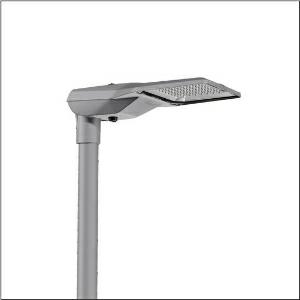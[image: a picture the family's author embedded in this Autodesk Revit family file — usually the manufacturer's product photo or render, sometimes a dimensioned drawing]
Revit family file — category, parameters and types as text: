
# Revit family: streetlight_sl_21_iq_midi___pl52_5xe3h31y08mb_cc6d
name_source: partatom
category: Lighting Fixtures
units: mm (PartAtom-declared; Revit-internal decimal feet)

## family parameters
Cut with Voids When Loaded = No
Host = Face
Light Source = No
Part Type = Normal
Room Calculation Point = No
Round Connector Dimension = Use Diameter
Shared = No

## types (1)
- --- (1 x LED, 18020 lm, 129.3 W, 3000K)
    Apparent Load = 129 VA
    CIE Flux Codes = 27 59 98 100 100
    Color Rendering = 70
    Color Temperature = 3000K
    Default Elevation = 1800 mm
    Description = Streetlight SL 21 iQ midi, mast luminaire, primary light control with lens, of PMMA, primary optical cover: cover, of toughened safety glass, transparent, light distribution: PL52, light emission: direct distribution, primary light characteristic: asymmetric, installation type: post-top, side-entry, LED, High Power LED, rated luminous flux: 18.020lm, luminous efficacy: 139lm/W, light colour: 730, colour temperature: 3000K, control gear: iQ-Street Remote, D4i with power reduction, control: pre-setting: logarithmic dimming characteristic, Street-Remote, Auto-Match, Temp-Guard, Lumen-Switch, Night-Set, Smart-Wire, Light-Fading, Desk-Remote (wireless, voltage-free reading and setting of iQ features in the workshop via application-optimized NFC function/RFID function), optimised constant luminous flux control (CLO 2.0), mains connection: 230..240V, AC, 50/60Hz, start of lifetime: 129W, end of service life: 142W, reduction: 56W, luminaire housing, of diecast aluminium, powder-coated, SITECO metallic grey (DB 702S), corrosivity category C5 high according to DIN EN ISO 12944, please order mast flange separately, inclination adjustable: 0°, 5°, 10°, 15°, sealing non-destructively replaceable, multi-level sealing system, length: 644mm, width: 335mm, height: 110mm, mast flange for spigot size: 42mm (side-entry): 5XC10008XM4, 60/48mm (side-entry/post-top): 5XC10108XM2, 76/60mm (side-entry/post-top): 5XC10108XM1, mounting height: 4..8m, Smart Interface below and above, protection rating (complete): IP66, insulation class (complete): insulation class II (safety insulation), certification: CE, ENEC, ENEC+, VDE, impact resistance: IK10, permissible operating ambient temperature for outdoor applications: -40..+50°C, standard-compliant lighting for roads and squares, packaging unit: 1 piece

Light Distribution: PL52
    Height = 111 mm
    Lamp = 1 x LED
    Lamp Light Flux = 18020 lm
    Lamp Power = 129.3 W
    Lamp count = 1
    Length = 644 mm
    Luminous efficacy = 139 lm/W
    Manufacturer = Siteco
    ModVariant = No
    Model = 5XE3H31Y08MB
    Number of Poles = 1
    OnlyDefault = Yes
    Power Factor = 1
    Product Name = Streetlight SL 21 iQ midi | PL52
    Product group = mast luminaire | pylon top
    ProductGroupID = 6100
    Protection Class = Protection class II
    Protection Degree = IP 66
    RLX_Detail_Level = 1
    RLX_Emergency_Light_Flux = 0 lm
    RLX_Emergency_Type = 0
    RLX_Emergency_Type_DB = No
    RlxData = <blob elided: 100813 chars, md5=255f2068>
    Socket = socket
    Standby Power = 0 W
    System Light Flux = 18021 lm
    System Power = 129 W
    Type Comments = factory setting: luminous flux: 100 % | dim-lin: 254 | 672 mA
    Type Image = l_1004304.jpg
    URL = http://relux.com
    VarID = @adj_115997
    Voltage = 0 V
    Weight = 0.00 kg
    Width = 336 mm

## geometry (parser evidence)
native form markers: Blend x4, Sweep x9
no freeform markers — native parametric forms only
